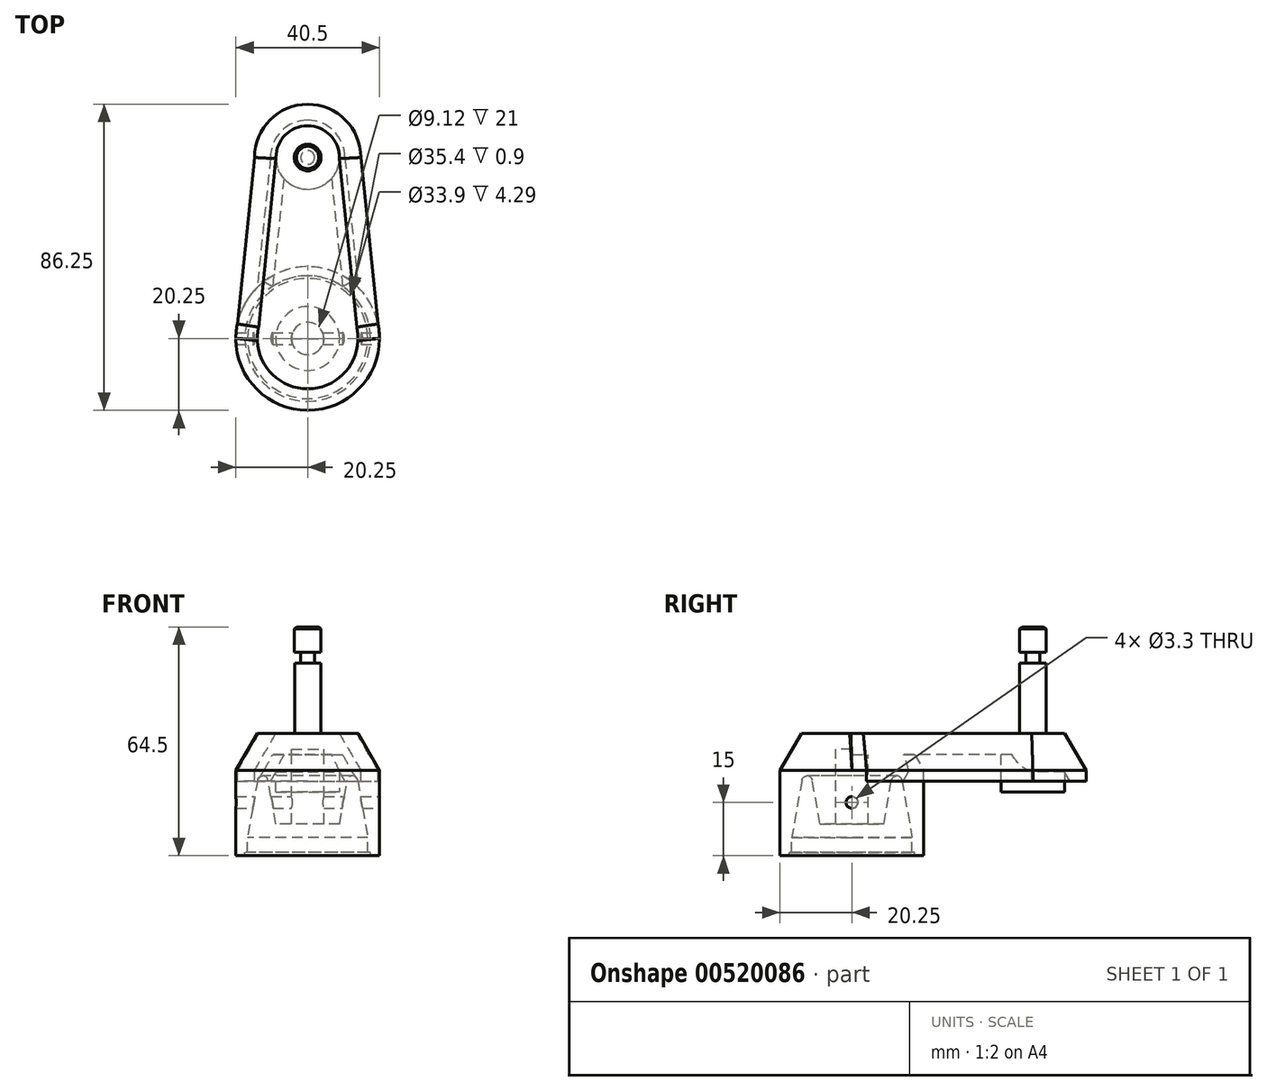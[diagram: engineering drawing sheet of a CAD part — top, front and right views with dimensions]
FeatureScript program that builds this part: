
annotation { "Feature Type Name" : "Feature", "Feature Type Description" : "" }
export const myFeature = defineFeature(function(context is Context, id is Id, definition is map)
    precondition{}
    {
        {
            var Q0;
            Q0=qCreatedBy(makeId("Right.planeOp"),FACE);
            var sketch = newSketch(context, id + "F0", { "sketchPlane" : qUnion([Q0])});
            skPoint(sketch, "E0", {"position": v(0, 11.5) * mm});
            skPoint(sketch, "E1", {"position": v(0, 10) * mm});
            skLineSegment(sketch, "E2", {"start": v(0, 10) * mm, "end": v(-1.52, 10) * mm});
            skLineSegment(sketch, "E3", {"start": v(-1.52, 10) * mm, "end": v(-1.52, 3) * mm});
            skLineSegment(sketch, "E4", {"start": v(-1.52, 3) * mm, "end": v(-3, 3) * mm});
            skLineSegment(sketch, "E5", {"start": v(-3, 3) * mm, "end": v(-3.72, 7.09) * mm});
            skLineSegment(sketch, "E6", {"start": v(-4.7, 7.09) * mm, "end": v(-5.65, 1.73) * mm});
            skLineSegment(sketch, "E7", {"start": v(-5.65, 1.73) * mm, "end": v(-5.65, 0.3) * mm});
            skLineSegment(sketch, "E8", {"start": v(-5.65, 0.3) * mm, "end": v(-5.9, 0.3) * mm});
            skLineSegment(sketch, "E9", {"start": v(-5.9, 0.3) * mm, "end": v(-5.9, 0) * mm});
            skLineSegment(sketch, "E10", {"start": v(-5.9, 0) * mm, "end": v(-6.75, 0) * mm});
            skLineSegment(sketch, "E11", {"start": v(-6.75, 0) * mm, "end": v(-6.75, 8) * mm});
            skLineSegment(sketch, "E12", {"start": v(-6.75, 8) * mm, "end": v(-4.73, 11.5) * mm});
            skLineSegment(sketch, "E13", {"start": v(-4.73, 11.5) * mm, "end": v(0, 11.5) * mm});
            skLineSegment(sketch, "E14", {"start": v(-5.65, 1.73) * mm, "end": v(-5.65, 11.5) * mm, "construction": true});
            skLineSegment(sketch, "E15", {"start": v(-3, 3) * mm, "end": v(-3, 11.5) * mm, "construction": true});
            skPoint(sketch, "E16.visualSharp", {"position": v(-4.21, 9.88) * mm});
            skArc(sketch, "E16.filletArc", {"start": v(-3.72, 7.09) * mm, "mid": v(-4.21, 7.5) * mm, "end": v(-4.7, 7.09) * mm});
            skLineSegment(sketch, "E17", {"start": v(-6.75, 8) * mm, "end": v(-6.75, 11.5) * mm, "construction": true});
            skLineSegment(sketch, "E18", {"start": v(0, 11.5) * mm, "end": v(0, 10) * mm});
            skSolve(sketch);
        }
        {
            var Q0;
            Q0=makeQuery(id+"F0.imprint","IMPRINT",FACE,{"disambiguationData":[TD([[makeQuery(id+"F0.imprint","IMPRINT",EDGE,{"derivedFrom":sQuery(id+"F0.wireOp",EDGE,"E2")}),-1.0]])]});
            var Q1;
            Q1=sQuery(id+"F0.wireOp",EDGE,"E18");
            revolve(context, id + "F1", {"entities" : qUnion([Q0]), "axis" : qUnion([Q1]), "revolveType" : RevolveType.FULL});
        }
        {
            var Q0;
            Q0=qCreatedBy(makeId("Right.planeOp"),FACE);
            var sketch = newSketch(context, id + "F2", { "sketchPlane" : qUnion([Q0])});
            skLineSegment(sketch, "E19", {"start": v(0, 0) * mm, "end": v(17, 0) * mm, "construction": true});
            skLineSegment(sketch, "E20", {"start": v(17, 0) * mm, "end": v(17, 11.5) * mm, "construction": true});
            skPoint(sketch, "E21", {"position": v(17, 9.5) * mm});
            skLineSegment(sketch, "E22", {"start": v(20.5, 7) * mm, "end": v(22, 7) * mm});
            skLineSegment(sketch, "E23", {"start": v(22, 7) * mm, "end": v(22, 8) * mm});
            skLineSegment(sketch, "E24", {"start": v(22, 8) * mm, "end": v(19.98, 11.5) * mm});
            skLineSegment(sketch, "E25", {"start": v(19.98, 11.5) * mm, "end": v(17, 11.5) * mm});
            skLineSegment(sketch, "E26", {"start": v(17, 9.5) * mm, "end": v(17, 11.5) * mm});
            skLineSegment(sketch, "E27", {"start": v(20.5, 7) * mm, "end": v(20.5, 0) * mm, "construction": true});
            skLineSegment(sketch, "E28", {"start": v(20.5, 7) * mm, "end": v(19.06, 9.5) * mm});
            skLineSegment(sketch, "E29", {"start": v(19.06, 9.5) * mm, "end": v(17, 9.5) * mm});
            skSolve(sketch);
        }
        {
            var Q0;
            Q0=qCreatedBy(makeId("Top.planeOp"),FACE);
            cPlane(context, id + "F3", {"entities" : qUnion([Q0]), "cplaneType" : CPlaneType.OFFSET, "offset" : 8 * mm, "width" : 150 * mm, "height" : 150 * mm});
        }
        {
            var Q0;
            Q0=qCreatedBy(id+"F3.planeOp",FACE);
            var sketch = newSketch(context, id + "F4", { "sketchPlane" : qUnion([Q0])});
            skArc(sketch, "E30", {"start": v(5, 17) * mm, "mid": v(3.54, 20.54) * mm, "end": v(0, 22) * mm});
            skPoint(sketch, "E31", {"position": v(0, 0) * mm});
            skLineSegment(sketch, "E32", {"start": v(-5, 17) * mm, "end": v(-6.75, 0) * mm});
            skLineSegment(sketch, "E33", {"start": v(5, 17) * mm, "end": v(6.75, 0) * mm});
            skLineSegment(sketch, "E34", {"start": v(0, 17) * mm, "end": v(0, 22) * mm, "construction": true});
            skLineSegment(sketch, "E35", {"start": v(0, 22) * mm, "end": v(0, 17) * mm, "construction": true});
            skArc(sketch, "E36", {"start": v(0, 22) * mm, "mid": v(-3.54, 20.54) * mm, "end": v(-5, 17) * mm});
            skSolve(sketch);
        }
        {
            var Q0;
            Q0=makeQuery(id+"F2.imprint","IMPRINT",FACE,{"disambiguationData":[TD([[makeQuery(id+"F2.imprint","IMPRINT",EDGE,{"derivedFrom":sQuery(id+"F2.wireOp",EDGE,"E22")}),1.0]])]});
            var Q1;
            Q1=sQuery(id+"F4.wireOp",EDGE,"E30");
            var Q2;
            Q2=sQuery(id+"F4.wireOp",EDGE,"E33");
            sweep(context, id + "F5", {"operationType" : NewBodyOperationType.ADD, "profiles" : qUnion([Q0]), "path" : qUnion([Q1, Q2])});
        }
        {
            var Q0;
            Q0=makeQuery(id+"F2.imprint","IMPRINT",FACE,{"disambiguationData":[TD([[makeQuery(id+"F2.imprint","IMPRINT",EDGE,{"derivedFrom":sQuery(id+"F2.wireOp",EDGE,"E22")}),1.0]])]});
            var Q1;
            Q1=sQuery(id+"F4.wireOp",EDGE,"E36");
            var Q2;
            Q2=sQuery(id+"F4.wireOp",EDGE,"E32");
            sweep(context, id + "F6", {"operationType" : NewBodyOperationType.ADD, "profiles" : qUnion([Q0]), "path" : qUnion([Q1, Q2])});
        }
        {
            var Q0;
            Q0=qCreatedBy(makeId("Front.planeOp"),FACE);
            var sketch = newSketch(context, id + "F7", { "sketchPlane" : qUnion([Q0])});
            skLineSegment(sketch, "E37.bottom", {"start": v(-2.5, 11.5) * mm, "end": v(2.5, 11.5) * mm});
            skLineSegment(sketch, "E37.top", {"start": v(-2.5, 9.5) * mm, "end": v(2.5, 9.5) * mm});
            skLineSegment(sketch, "E37.left", {"start": v(-2.5, 11.5) * mm, "end": v(-2.5, 9.5) * mm});
            skLineSegment(sketch, "E37.right", {"start": v(2.5, 11.5) * mm, "end": v(2.5, 9.5) * mm});
            skSolve(sketch);
        }
        {
            var Q0;
            Q0=makeQuery(id+"F7.imprint","IMPRINT",FACE,{"disambiguationData":[TD([[makeQuery(id+"F7.imprint","IMPRINT",EDGE,{"derivedFrom":sQuery(id+"F7.wireOp",EDGE,"E37.bottom")}),-1.0]])]});
            extrude(context, id + "F8", {"entities" : qUnion([Q0]), "operationType" : NewBodyOperationType.ADD, "oppositeDirection" : true, "depth" : 17 * mm});
        }
        {
            var Q0;
            {var subQ0=sQuery(id+"F2.wireOp",EDGE,"E25");Q0=makeQuery(id+"F8.boolean.opBoolean","MERGE",FACE,{"derivedFrom":[makeQuery(id+"F6.boolean.opBoolean","MERGE",FACE,{"derivedFrom":[makeQuery(id+"F5.boolean.opBoolean","MERGE",FACE,{"derivedFrom":[makeQuery(id+"F1.opRevolve","SWEPT_FACE",FACE,{"disambiguationData":[OSD([sQuery(id+"F0.wireOp",EDGE,"E13")])]}),makeQuery(id+"F5.opSweep","MID_CAP_FACE",FACE,{"disambiguationData":[OSD([subQ0,sQuery(id+"F4.wireOp",VERTEX,"E33.start")])],"capPos":1.0})]}),makeQuery(id+"F6.opSweep","MID_CAP_FACE",FACE,{"disambiguationData":[OSD([subQ0,sQuery(id+"F4.wireOp",VERTEX,"E32.start")])],"capPos":1.0})]}),makeQuery(id+"F8.opExtrude","SWEPT_FACE",FACE,{"disambiguationData":[OSD([sQuery(id+"F7.wireOp",EDGE,"E37.bottom")])]})]});}
            var sketch = newSketch(context, id + "F9", { "sketchPlane" : qUnion([Q0])});
            skLineSegment(sketch, "E38", {"start": v(0, 0) * mm, "end": v(0, 17) * mm, "construction": true});
            skCircle(sketch, "E39", {"center": v(0, 17) * mm, "radius": 2.98 * mm});
            skCircle(sketch, "E40", {"center": v(0, 17) * mm, "radius": 1.23 * mm});
            skSolve(sketch);
        }
        {
            var Q0;
            {var subQ0=sQuery(id+"F2.wireOp",EDGE,"E24");var subQ1=sQuery(id+"F2.wireOp",EDGE,"E25");var subQ2=sQuery(id+"F4.wireOp",EDGE,"E36");var subQ3=makeQuery(id+"F6.opSweep","SWEPT_EDGE",EDGE,{"disambiguationData":[OSD([subQ0,subQ1,subQ2]),OD(1.0)]});var subQ4=makeQuery(id+"F9.imprint","IMPRINT",EDGE,{"derivedFrom":subQ3});var subQ12=sQuery(id+"F4.wireOp",EDGE,"E30");var subQ13=makeQuery(id+"F5.opSweep","SWEPT_EDGE",EDGE,{"disambiguationData":[OSD([subQ0,subQ1,subQ12]),OD(1.0)]});var subQ14=makeQuery(id+"F9.imprint","IMPRINT",EDGE,{"derivedFrom":subQ13});Q0=qUnion([makeQuery(id+"F9.imprint","IMPRINT",FACE,{"disambiguationData":[TD([[subQ4,-1.0]])]}),makeQuery(id+"F9.imprint","IMPRINT",FACE,{"disambiguationData":[TD([[subQ14,1.0]])]}),makeQuery(id+"F9.imprint","IMPRINT",FACE,{"disambiguationData":[TD([[makeQuery(id+"F9.imprint","IMPRINT",EDGE,{"derivedFrom":sQuery(id+"F9.wireOp",EDGE,"E40")}),-1.0]])]})]);}
            var Q1;
            Q1=makeQuery(id+"F9.imprint","IMPRINT",FACE,{"disambiguationData":[TD([[makeQuery(id+"F9.imprint","IMPRINT",EDGE,{"derivedFrom":sQuery(id+"F9.wireOp",EDGE,"E40")}),1.0]])]});
            extrude(context, id + "F10", {"entities" : qUnion([Q0, Q1]), "operationType" : NewBodyOperationType.ADD, "oppositeDirection" : true, "depth" : 5.5 * mm});
        }
        {
            var Q0;
            Q0=makeQuery(id+"F9.imprint","IMPRINT",FACE,{"disambiguationData":[TD([[makeQuery(id+"F9.imprint","IMPRINT",EDGE,{"derivedFrom":sQuery(id+"F9.wireOp",EDGE,"E40")}),1.0]])]});
            extrude(context, id + "F11", {"entities" : qUnion([Q0]), "operationType" : NewBodyOperationType.ADD, "depth" : 6.6 * mm});
        }
        {
            var Q0;
            Q0=makeQuery(id+"F11.opExtrude","CAP_FACE",FACE,{"disambiguationData":[OSD([sQuery(id+"F9.wireOp",EDGE,"E40")])],"isStart":false});
            var sketch = newSketch(context, id + "F12", { "sketchPlane" : qUnion([Q0])});
            skCircle(sketch, "E41", {"center": v(0, 17) * mm, "radius": 0.65 * mm});
            skSolve(sketch);
        }
        {
            var Q0;
            Q0=makeQuery(id+"F12.imprint","IMPRINT",FACE,{"disambiguationData":[TD([[makeQuery(id+"F12.imprint","IMPRINT",EDGE,{"derivedFrom":sQuery(id+"F12.wireOp",EDGE,"E41")}),1.0]])]});
            extrude(context, id + "F13", {"entities" : qUnion([Q0]), "operationType" : NewBodyOperationType.ADD, "depth" : 1 * mm});
        }
        {
            var Q0;
            Q0=makeQuery(id+"F13.opExtrude","CAP_FACE",FACE,{"disambiguationData":[OSD([sQuery(id+"F12.wireOp",EDGE,"E41")])],"isStart":false});
            var sketch = newSketch(context, id + "F14", { "sketchPlane" : qUnion([Q0])});
            skCircle(sketch, "E42", {"center": v(0, 17) * mm, "radius": 1.25 * mm});
            skSolve(sketch);
        }
        {
            var Q0;
            {var subQ0=makeQuery(id+"F14.imprint","IMPRINT",EDGE,{"derivedFrom":makeQuery(id+"F13.opExtrude","CAP_EDGE",EDGE,{"disambiguationData":[OSD([sQuery(id+"F12.wireOp",EDGE,"E41")])],"isStart":false})});Q0=qUnion([makeQuery(id+"F14.imprint","IMPRINT",FACE,{"disambiguationData":[TD([[makeQuery(id+"F14.imprint","IMPRINT",EDGE,{"derivedFrom":sQuery(id+"F14.wireOp",EDGE,"E42")}),1.0]])]}),makeQuery(id+"F14.imprint","IMPRINT",FACE,{"disambiguationData":[TD([[subQ0,1.0]])]})]);}
            extrude(context, id + "F15", {"entities" : qUnion([Q0]), "operationType" : NewBodyOperationType.ADD, "depth" : 2.4 * mm});
        }
        {
            var Q0;
            Q0=makeQuery(id+"F15.opExtrude","CAP_EDGE",EDGE,{"disambiguationData":[OSD([sQuery(id+"F14.wireOp",EDGE,"E42")])],"isStart":false});
            chamfer(context, id + "F16", {"entities" : qUnion([Q0]), "width" : 0.2 * mm, "tangentPropagation" : true});
        }
        {
            var Q0;
            Q0=makeQuery(id+"F1.opRevolve","SWEPT_BODY",BODY,{"disambiguationData":[OSD([sQuery(id+"F0.wireOp",EDGE,"E2"),sQuery(id+"F0.wireOp",EDGE,"E3"),sQuery(id+"F0.wireOp",EDGE,"E4"),sQuery(id+"F0.wireOp",EDGE,"E5"),sQuery(id+"F0.wireOp",EDGE,"E6"),sQuery(id+"F0.wireOp",EDGE,"E7"),sQuery(id+"F0.wireOp",EDGE,"E8"),sQuery(id+"F0.wireOp",EDGE,"E9"),sQuery(id+"F0.wireOp",EDGE,"E10"),sQuery(id+"F0.wireOp",EDGE,"E11"),sQuery(id+"F0.wireOp",EDGE,"E12"),sQuery(id+"F0.wireOp",EDGE,"E13"),sQuery(id+"F0.wireOp",EDGE,"E16.filletArc"),sQuery(id+"F0.wireOp",EDGE,"E18")])]});
            var Q1;
            Q1=qCreatedBy(makeId("Origin.pointOp"),VERTEX);
            transform(context, id + "F17", {"entities" : qUnion([Q0]), "transformType" : TransformType.SCALE_UNIFORMLY, "scale" : 3, "makeCopy" : false, "scalePoint" : qUnion([Q1])});
        }
        {
            var Q0;
            Q0=qCreatedBy(makeId("Right.planeOp"),FACE);
            var sketch = newSketch(context, id + "F18", { "sketchPlane" : qUnion([Q0])});
            skCircle(sketch, "E43", {"center": v(0, 15) * mm, "radius": 1.65 * mm});
            skSolve(sketch);
        }
        {
            var Q0;
            Q0=qSketchRegion(id+"F18",true);
            extrude(context, id + "F19", {"entities" : qUnion([Q0]), "operationType" : NewBodyOperationType.REMOVE, "endBound" : BoundingType.SYMMETRIC, "oppositeDirection" : true, "depth" : 42 * mm});
        }
    });
